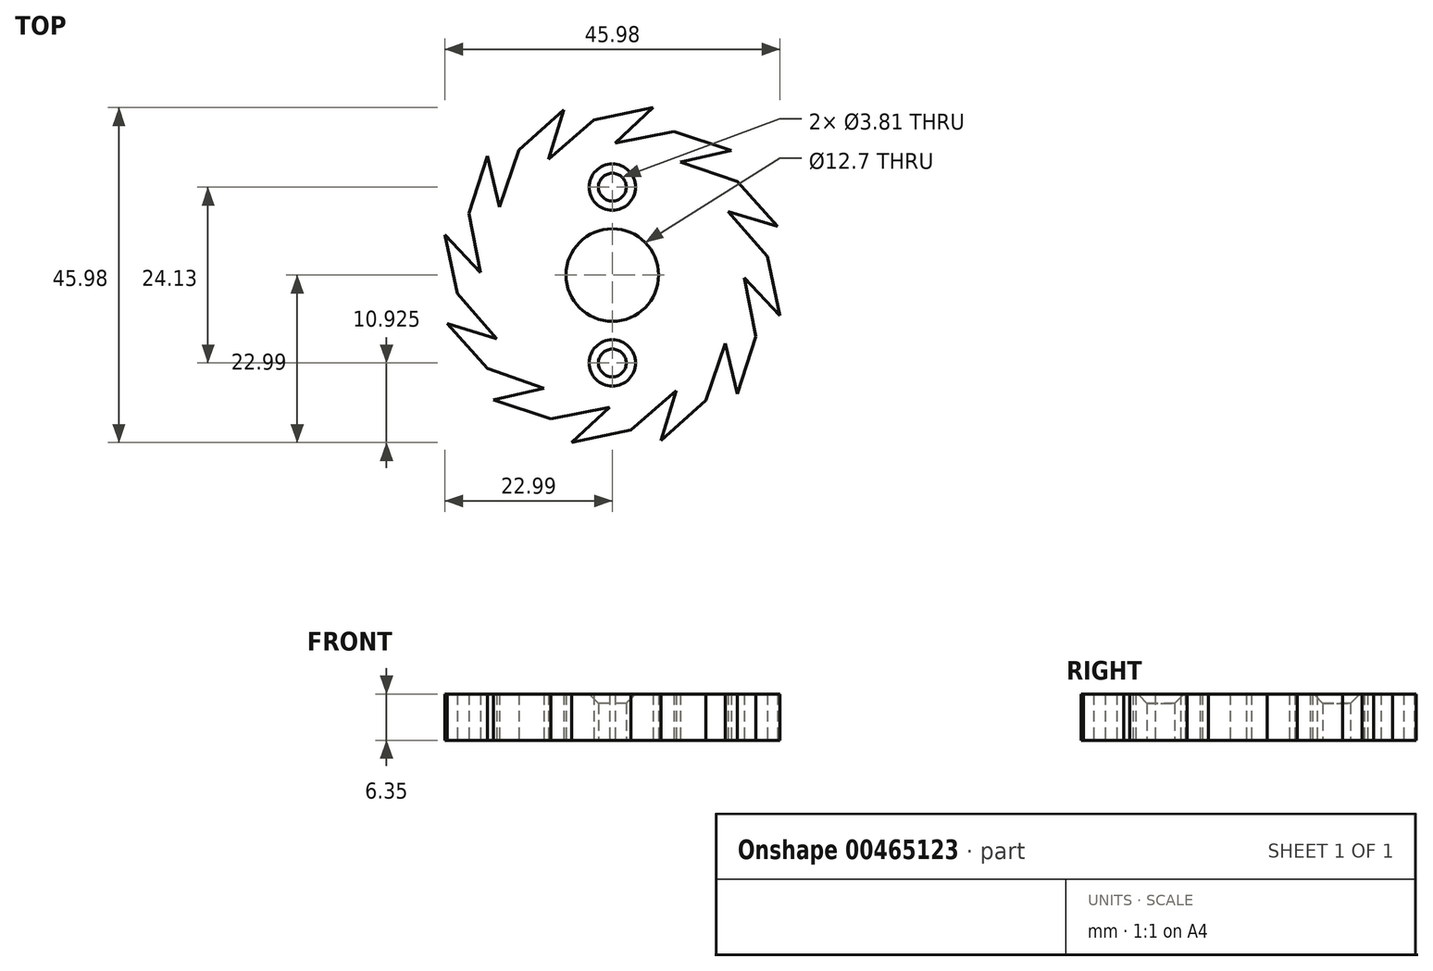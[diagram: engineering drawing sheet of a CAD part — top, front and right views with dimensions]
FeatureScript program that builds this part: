
annotation { "Feature Type Name" : "Feature", "Feature Type Description" : "" }
export const myFeature = defineFeature(function(context is Context, id is Id, definition is map)
    precondition{}
    {
        {
            var Q0;
            Q0=qCreatedBy(makeId("Top.planeOp"),FACE);
            var sketch = newSketch(context, id + "F0", { "sketchPlane" : qUnion([Q0])});
            skCircle(sketch, "E0", {"center": v(0, 0) * mm, "radius": 17.78 * mm});
            skPoint(sketch, "E1.center", {"position": v(2.36, 2.72) * mm});
            skCircle(sketch, "E2", {"center": v(0, 0) * mm, "radius": 6.35 * mm});
            skLineSegment(sketch, "E3", {"start": v(0, 6.35) * mm, "end": v(0, 17.78) * mm});
            skLineSegment(sketch, "E4", {"start": v(0, -6.35) * mm, "end": v(0, -17.78) * mm});
            skCircle(sketch, "E5", {"center": v(0, 12.06) * mm, "radius": 1.9 * mm});
            skCircle(sketch, "E6", {"center": v(0, -12.07) * mm, "radius": 1.9 * mm});
            skLineSegment(sketch, "E7", {"start": v(0, 17.78) * mm, "end": v(5.56, 22.99) * mm});
            skLineSegment(sketch, "E8", {"start": v(5.56, 22.99) * mm, "end": v(-2.54, 21.28) * mm});
            skLineSegment(sketch, "E9", {"start": v(-2.54, 21.28) * mm, "end": v(-10.44, 14.4) * mm});
            skLineSegment(sketch, "E10.1.0", {"start": v(-8.89, 15.4) * mm, "end": v(-6.67, 22.69) * mm});
            skLineSegment(sketch, "E10.1.1", {"start": v(-6.67, 22.69) * mm, "end": v(-12.84, 17.16) * mm});
            skLineSegment(sketch, "E10.1.2", {"start": v(-12.84, 17.16) * mm, "end": v(-16.24, 7.25) * mm});
            skLineSegment(sketch, "E10.2.0", {"start": v(-15.4, 8.89) * mm, "end": v(-17.12, 16.31) * mm});
            skLineSegment(sketch, "E10.2.1", {"start": v(-17.12, 16.31) * mm, "end": v(-19.7, 8.44) * mm});
            skLineSegment(sketch, "E10.2.2", {"start": v(-19.7, 8.44) * mm, "end": v(-17.68, -1.84) * mm});
            skLineSegment(sketch, "E10.3.0", {"start": v(-17.78, 0) * mm, "end": v(-22.99, 5.56) * mm});
            skLineSegment(sketch, "E10.3.1", {"start": v(-22.99, 5.56) * mm, "end": v(-21.28, -2.54) * mm});
            skLineSegment(sketch, "E10.3.2", {"start": v(-21.28, -2.54) * mm, "end": v(-14.4, -10.44) * mm});
            skLineSegment(sketch, "E10.4.0", {"start": v(-15.4, -8.89) * mm, "end": v(-22.69, -6.67) * mm});
            skLineSegment(sketch, "E10.4.1", {"start": v(-22.69, -6.67) * mm, "end": v(-17.16, -12.84) * mm});
            skLineSegment(sketch, "E10.4.2", {"start": v(-17.16, -12.84) * mm, "end": v(-7.25, -16.24) * mm});
            skLineSegment(sketch, "E10.5.0", {"start": v(-8.89, -15.4) * mm, "end": v(-16.31, -17.12) * mm});
            skLineSegment(sketch, "E10.5.1", {"start": v(-16.31, -17.12) * mm, "end": v(-8.44, -19.7) * mm});
            skLineSegment(sketch, "E10.5.2", {"start": v(-8.44, -19.7) * mm, "end": v(1.84, -17.68) * mm});
            skLineSegment(sketch, "E10.6.0", {"start": v(0, -17.78) * mm, "end": v(-5.56, -22.99) * mm});
            skLineSegment(sketch, "E10.6.1", {"start": v(-5.56, -22.99) * mm, "end": v(2.54, -21.28) * mm});
            skLineSegment(sketch, "E10.6.2", {"start": v(2.54, -21.28) * mm, "end": v(10.44, -14.4) * mm});
            skLineSegment(sketch, "E10.7.0", {"start": v(8.89, -15.4) * mm, "end": v(6.67, -22.69) * mm});
            skLineSegment(sketch, "E10.7.1", {"start": v(6.67, -22.69) * mm, "end": v(12.84, -17.16) * mm});
            skLineSegment(sketch, "E10.7.2", {"start": v(12.84, -17.16) * mm, "end": v(16.24, -7.25) * mm});
            skLineSegment(sketch, "E10.8.0", {"start": v(15.4, -8.9) * mm, "end": v(17.12, -16.31) * mm});
            skLineSegment(sketch, "E10.8.1", {"start": v(17.12, -16.31) * mm, "end": v(19.7, -8.44) * mm});
            skLineSegment(sketch, "E10.8.2", {"start": v(19.7, -8.44) * mm, "end": v(17.68, 1.84) * mm});
            skLineSegment(sketch, "E10.9.0", {"start": v(17.78, 0) * mm, "end": v(22.99, -5.56) * mm});
            skLineSegment(sketch, "E10.9.1", {"start": v(22.99, -5.56) * mm, "end": v(21.28, 2.54) * mm});
            skLineSegment(sketch, "E10.9.2", {"start": v(21.28, 2.54) * mm, "end": v(14.4, 10.44) * mm});
            skLineSegment(sketch, "E10.10.0", {"start": v(15.4, 8.89) * mm, "end": v(22.69, 6.67) * mm});
            skLineSegment(sketch, "E10.10.1", {"start": v(22.69, 6.67) * mm, "end": v(17.16, 12.84) * mm});
            skLineSegment(sketch, "E10.10.2", {"start": v(17.16, 12.84) * mm, "end": v(7.25, 16.24) * mm});
            skLineSegment(sketch, "E10.11.0", {"start": v(8.9, 15.4) * mm, "end": v(16.31, 17.12) * mm});
            skLineSegment(sketch, "E10.11.1", {"start": v(16.31, 17.12) * mm, "end": v(8.44, 19.7) * mm});
            skLineSegment(sketch, "E10.11.2", {"start": v(8.44, 19.7) * mm, "end": v(-1.84, 17.68) * mm});
            skSolve(sketch);
        }
        {
            var Q0;
            {var subQ3=sQuery(id+"F0.wireOp",EDGE,"E1.5.0");var subQ7=sQuery(id+"F0.wireOp",EDGE,"E0");var subQ8=makeQuery(id+"F0.imprint","INTERSECT",VERTEX,{"derivedFrom":[subQ7,subQ3]});Q0=makeQuery(id+"F0.imprint","IMPRINT",FACE,{"disambiguationData":[TD([[makeQuery(id+"F0.imprint","IMPRINT",EDGE,{"disambiguationData":[TD([[subQ8,-1.0]])],"derivedFrom":subQ7}),-1.0]])]});}
            var Q1;
            {var subQ3=sQuery(id+"F0.wireOp",EDGE,"E1.1.0");var subQ7=sQuery(id+"F0.wireOp",EDGE,"E0");var subQ8=makeQuery(id+"F0.imprint","INTERSECT",VERTEX,{"derivedFrom":[subQ7,subQ3]});Q1=makeQuery(id+"F0.imprint","IMPRINT",FACE,{"disambiguationData":[TD([[makeQuery(id+"F0.imprint","IMPRINT",EDGE,{"disambiguationData":[TD([[subQ8,-1.0]])],"derivedFrom":subQ7}),-1.0]])]});}
            var Q2;
            {var subQ3=sQuery(id+"F0.wireOp",EDGE,"XDNQqefp-l6QH-Php1-q7ec-htYRLLk1gTAw");var subQ5=sQuery(id+"F0.wireOp",EDGE,"E0");var subQ6=makeQuery(id+"F0.imprint","INTERSECT",VERTEX,{"derivedFrom":[subQ5,subQ3]});Q2=makeQuery(id+"F0.imprint","IMPRINT",FACE,{"disambiguationData":[TD([[makeQuery(id+"F0.imprint","IMPRINT",EDGE,{"disambiguationData":[TD([[subQ6,-1.0]])],"derivedFrom":subQ5}),-1.0]])]});}
            var Q3;
            {var subQ3=sQuery(id+"F0.wireOp",EDGE,"E1.7.0");var subQ5=sQuery(id+"F0.wireOp",EDGE,"E0");var subQ6=makeQuery(id+"F0.imprint","INTERSECT",VERTEX,{"derivedFrom":[subQ5,subQ3]});Q3=makeQuery(id+"F0.imprint","IMPRINT",FACE,{"disambiguationData":[TD([[makeQuery(id+"F0.imprint","IMPRINT",EDGE,{"disambiguationData":[TD([[subQ6,-1.0]])],"derivedFrom":subQ5}),-1.0]])]});}
            var Q4;
            {var subQ5=sQuery(id+"F0.wireOp",EDGE,"E1.8.0");var subQ6=sQuery(id+"F0.wireOp",EDGE,"E0");var subQ7=makeQuery(id+"F0.imprint","INTERSECT",VERTEX,{"derivedFrom":[subQ6,subQ5]});Q4=makeQuery(id+"F0.imprint","IMPRINT",FACE,{"disambiguationData":[TD([[makeQuery(id+"F0.imprint","IMPRINT",EDGE,{"disambiguationData":[TD([[subQ7,-1.0]])],"derivedFrom":subQ6}),-1.0]])]});}
            var Q5;
            {var subQ0=sQuery(id+"F0.wireOp",EDGE,"E1.9.0");var subQ1=sQuery(id+"F0.wireOp",EDGE,"E0");var subQ2=makeQuery(id+"F0.imprint","INTERSECT",VERTEX,{"derivedFrom":[subQ1,subQ0]});Q5=makeQuery(id+"F0.imprint","IMPRINT",FACE,{"disambiguationData":[TD([[makeQuery(id+"F0.imprint","IMPRINT",EDGE,{"disambiguationData":[TD([[subQ2,1.0]])],"derivedFrom":subQ0}),-1.0]])]});}
            var Q6;
            {var subQ3=sQuery(id+"F0.wireOp",EDGE,"E1.1.1");var subQ5=sQuery(id+"F0.wireOp",EDGE,"E0");var subQ6=makeQuery(id+"F0.imprint","INTERSECT",VERTEX,{"derivedFrom":[subQ5,subQ3]});Q6=makeQuery(id+"F0.imprint","IMPRINT",FACE,{"disambiguationData":[TD([[makeQuery(id+"F0.imprint","IMPRINT",EDGE,{"disambiguationData":[TD([[subQ6,1.0]])],"derivedFrom":subQ5}),-1.0]])]});}
            var Q7;
            {var subQ0=sQuery(id+"F0.wireOp",EDGE,"E0");var subQ11=makeQuery(id+"F0.imprint","INTERSECT",VERTEX,{"derivedFrom":[subQ0,sQuery(id+"F0.wireOp",EDGE,"E1.7.0")]});Q7=makeQuery(id+"F0.imprint","IMPRINT",FACE,{"disambiguationData":[TD([[makeQuery(id+"F0.imprint","IMPRINT",EDGE,{"disambiguationData":[TD([[subQ11,-1.0]])],"derivedFrom":subQ0}),1.0]])]});}
            var Q8;
            {var subQ3=sQuery(id+"F0.wireOp",EDGE,"E1.2.0");var subQ7=sQuery(id+"F0.wireOp",EDGE,"E0");var subQ8=makeQuery(id+"F0.imprint","INTERSECT",VERTEX,{"derivedFrom":[subQ7,subQ3]});Q8=makeQuery(id+"F0.imprint","IMPRINT",FACE,{"disambiguationData":[TD([[makeQuery(id+"F0.imprint","IMPRINT",EDGE,{"disambiguationData":[TD([[subQ8,-1.0]])],"derivedFrom":subQ7}),-1.0]])]});}
            var Q9;
            {var subQ0=sQuery(id+"F0.wireOp",EDGE,"E0");var subQ15=makeQuery(id+"F0.imprint","INTERSECT",VERTEX,{"derivedFrom":[subQ0,sQuery(id+"F0.wireOp",EDGE,"E1.1.1")]});Q9=makeQuery(id+"F0.imprint","IMPRINT",FACE,{"disambiguationData":[TD([[makeQuery(id+"F0.imprint","IMPRINT",EDGE,{"disambiguationData":[TD([[subQ15,1.0]])],"derivedFrom":subQ0}),1.0]])]});}
            var Q10;
            {var subQ3=sQuery(id+"F0.wireOp",EDGE,"E1.6.0");var subQ5=sQuery(id+"F0.wireOp",EDGE,"E0");var subQ6=makeQuery(id+"F0.imprint","INTERSECT",VERTEX,{"derivedFrom":[subQ5,subQ3]});Q10=makeQuery(id+"F0.imprint","IMPRINT",FACE,{"disambiguationData":[TD([[makeQuery(id+"F0.imprint","IMPRINT",EDGE,{"disambiguationData":[TD([[subQ6,-1.0]])],"derivedFrom":subQ5}),-1.0]])]});}
            var Q11;
            {var subQ5=sQuery(id+"F0.wireOp",EDGE,"E1.4.0");var subQ6=sQuery(id+"F0.wireOp",EDGE,"E0");var subQ7=makeQuery(id+"F0.imprint","INTERSECT",VERTEX,{"derivedFrom":[subQ6,subQ5]});Q11=makeQuery(id+"F0.imprint","IMPRINT",FACE,{"disambiguationData":[TD([[makeQuery(id+"F0.imprint","IMPRINT",EDGE,{"disambiguationData":[TD([[subQ7,-1.0]])],"derivedFrom":subQ6}),-1.0]])]});}
            var Q12;
            {var subQ3=sQuery(id+"F0.wireOp",EDGE,"E1.3.0");var subQ5=sQuery(id+"F0.wireOp",EDGE,"E0");var subQ6=makeQuery(id+"F0.imprint","INTERSECT",VERTEX,{"derivedFrom":[subQ5,subQ3]});Q12=makeQuery(id+"F0.imprint","IMPRINT",FACE,{"disambiguationData":[TD([[makeQuery(id+"F0.imprint","IMPRINT",EDGE,{"disambiguationData":[TD([[subQ6,-1.0]])],"derivedFrom":subQ5}),-1.0]])]});}
            var Q13;
            {var subQ0=sQuery(id+"F0.wireOp",EDGE,"E1.4.0");var subQ1=sQuery(id+"F0.wireOp",EDGE,"E0");var subQ2=makeQuery(id+"F0.imprint","INTERSECT",VERTEX,{"derivedFrom":[subQ1,subQ0]});Q13=makeQuery(id+"F0.imprint","IMPRINT",FACE,{"disambiguationData":[TD([[makeQuery(id+"F0.imprint","IMPRINT",EDGE,{"disambiguationData":[TD([[subQ2,1.0]])],"derivedFrom":subQ1}),-1.0]])]});}
            var Q14;
            {var subQ0=sQuery(id+"F0.wireOp",EDGE,"E1.1.0");var subQ1=sQuery(id+"F0.wireOp",EDGE,"E0");var subQ2=makeQuery(id+"F0.imprint","INTERSECT",VERTEX,{"derivedFrom":[subQ1,subQ0]});Q14=makeQuery(id+"F0.imprint","IMPRINT",FACE,{"disambiguationData":[TD([[makeQuery(id+"F0.imprint","IMPRINT",EDGE,{"disambiguationData":[TD([[subQ2,1.0]])],"derivedFrom":subQ1}),-1.0]])]});}
            var Q15;
            {var subQ0=sQuery(id+"F0.wireOp",EDGE,"E1.2.0");var subQ1=sQuery(id+"F0.wireOp",EDGE,"E0");var subQ2=makeQuery(id+"F0.imprint","INTERSECT",VERTEX,{"derivedFrom":[subQ1,subQ0]});Q15=makeQuery(id+"F0.imprint","IMPRINT",FACE,{"disambiguationData":[TD([[makeQuery(id+"F0.imprint","IMPRINT",EDGE,{"disambiguationData":[TD([[subQ2,1.0]])],"derivedFrom":subQ1}),-1.0]])]});}
            var Q16;
            {var subQ0=sQuery(id+"F0.wireOp",EDGE,"E1.8.0");var subQ1=sQuery(id+"F0.wireOp",EDGE,"E0");var subQ2=makeQuery(id+"F0.imprint","INTERSECT",VERTEX,{"derivedFrom":[subQ1,subQ0]});Q16=makeQuery(id+"F0.imprint","IMPRINT",FACE,{"disambiguationData":[TD([[makeQuery(id+"F0.imprint","IMPRINT",EDGE,{"disambiguationData":[TD([[subQ2,1.0]])],"derivedFrom":subQ1}),-1.0]])]});}
            var Q17;
            {var subQ0=sQuery(id+"F0.wireOp",EDGE,"E1.9.0");var subQ1=sQuery(id+"F0.wireOp",EDGE,"E0");var subQ2=makeQuery(id+"F0.imprint","INTERSECT",VERTEX,{"derivedFrom":[subQ1,subQ0]});Q17=makeQuery(id+"F0.imprint","IMPRINT",FACE,{"disambiguationData":[TD([[makeQuery(id+"F0.imprint","IMPRINT",EDGE,{"disambiguationData":[TD([[subQ2,1.0]])],"derivedFrom":subQ1}),-1.0]])]});}
            var Q18;
            {var subQ1=sQuery(id+"F0.wireOp",EDGE,"E0");var subQ3=sQuery(id+"F0.wireOp",EDGE,"E1.10.0");var subQ4=makeQuery(id+"F0.imprint","INTERSECT",VERTEX,{"derivedFrom":[subQ1,subQ3]});Q18=makeQuery(id+"F0.imprint","IMPRINT",FACE,{"disambiguationData":[TD([[makeQuery(id+"F0.imprint","IMPRINT",EDGE,{"disambiguationData":[TD([[subQ4,1.0]])],"derivedFrom":subQ3}),1.0]])]});}
            var Q19;
            {var subQ0=sQuery(id+"F0.wireOp",EDGE,"XDNQqefp-l6QH-Php1-q7ec-htYRLLk1gTAw");var subQ1=sQuery(id+"F0.wireOp",EDGE,"E0");var subQ2=makeQuery(id+"F0.imprint","INTERSECT",VERTEX,{"derivedFrom":[subQ1,subQ0]});Q19=makeQuery(id+"F0.imprint","IMPRINT",FACE,{"disambiguationData":[TD([[makeQuery(id+"F0.imprint","IMPRINT",EDGE,{"disambiguationData":[TD([[subQ2,1.0]])],"derivedFrom":subQ1}),-1.0]])]});}
            var Q20;
            {var subQ0=sQuery(id+"F0.wireOp",EDGE,"E1.6.0");var subQ1=sQuery(id+"F0.wireOp",EDGE,"E0");var subQ2=makeQuery(id+"F0.imprint","INTERSECT",VERTEX,{"derivedFrom":[subQ1,subQ0]});Q20=makeQuery(id+"F0.imprint","IMPRINT",FACE,{"disambiguationData":[TD([[makeQuery(id+"F0.imprint","IMPRINT",EDGE,{"disambiguationData":[TD([[subQ2,1.0]])],"derivedFrom":subQ1}),-1.0]])]});}
            var Q21;
            {var subQ0=sQuery(id+"F0.wireOp",EDGE,"E1.5.0");var subQ1=sQuery(id+"F0.wireOp",EDGE,"E0");var subQ2=makeQuery(id+"F0.imprint","INTERSECT",VERTEX,{"derivedFrom":[subQ1,subQ0]});Q21=makeQuery(id+"F0.imprint","IMPRINT",FACE,{"disambiguationData":[TD([[makeQuery(id+"F0.imprint","IMPRINT",EDGE,{"disambiguationData":[TD([[subQ2,1.0]])],"derivedFrom":subQ1}),-1.0]])]});}
            var Q22;
            {var subQ0=sQuery(id+"F0.wireOp",EDGE,"E1.3.0");var subQ1=sQuery(id+"F0.wireOp",EDGE,"E0");var subQ2=makeQuery(id+"F0.imprint","INTERSECT",VERTEX,{"derivedFrom":[subQ1,subQ0]});Q22=makeQuery(id+"F0.imprint","IMPRINT",FACE,{"disambiguationData":[TD([[makeQuery(id+"F0.imprint","IMPRINT",EDGE,{"disambiguationData":[TD([[subQ2,1.0]])],"derivedFrom":subQ1}),-1.0]])]});}
            var Q23;
            {var subQ0=sQuery(id+"F0.wireOp",EDGE,"E1.7.0");var subQ1=sQuery(id+"F0.wireOp",EDGE,"E0");var subQ2=makeQuery(id+"F0.imprint","INTERSECT",VERTEX,{"derivedFrom":[subQ1,subQ0]});Q23=makeQuery(id+"F0.imprint","IMPRINT",FACE,{"disambiguationData":[TD([[makeQuery(id+"F0.imprint","IMPRINT",EDGE,{"disambiguationData":[TD([[subQ2,1.0]])],"derivedFrom":subQ1}),-1.0]])]});}
            var Q24;
            {var subQ3=sQuery(id+"F0.wireOp",EDGE,"8bfdb414-f59d-4248-bad3-29c6685c9aad.1.0");var subQ5=sQuery(id+"F0.wireOp",EDGE,"E0");var subQ6=makeQuery(id+"F0.imprint","INTERSECT",VERTEX,{"derivedFrom":[subQ5,subQ3]});Q24=makeQuery(id+"F0.imprint","IMPRINT",FACE,{"disambiguationData":[TD([[makeQuery(id+"F0.imprint","IMPRINT",EDGE,{"disambiguationData":[TD([[subQ6,1.0]])],"derivedFrom":subQ5}),-1.0]])]});}
            var Q25;
            {var subQ3=sQuery(id+"F0.wireOp",EDGE,"8bfdb414-f59d-4248-bad3-29c6685c9aad.10.1");var subQ5=sQuery(id+"F0.wireOp",EDGE,"E0");var subQ6=makeQuery(id+"F0.imprint","INTERSECT",VERTEX,{"derivedFrom":[subQ5,subQ3]});Q25=makeQuery(id+"F0.imprint","IMPRINT",FACE,{"disambiguationData":[TD([[makeQuery(id+"F0.imprint","IMPRINT",EDGE,{"disambiguationData":[TD([[subQ6,1.0]])],"derivedFrom":subQ3}),-1.0]])]});}
            var Q26;
            {var subQ3=sQuery(id+"F0.wireOp",EDGE,"8bfdb414-f59d-4248-bad3-29c6685c9aad.9.1");var subQ5=sQuery(id+"F0.wireOp",EDGE,"E0");var subQ6=makeQuery(id+"F0.imprint","INTERSECT",VERTEX,{"derivedFrom":[subQ5,subQ3]});Q26=makeQuery(id+"F0.imprint","IMPRINT",FACE,{"disambiguationData":[TD([[makeQuery(id+"F0.imprint","IMPRINT",EDGE,{"disambiguationData":[TD([[subQ6,-1.0]])],"derivedFrom":subQ5}),-1.0]])]});}
            var Q27;
            {var subQ5=sQuery(id+"F0.wireOp",EDGE,"8bfdb414-f59d-4248-bad3-29c6685c9aad.8.1");var subQ7=sQuery(id+"F0.wireOp",EDGE,"E0");var subQ8=makeQuery(id+"F0.imprint","INTERSECT",VERTEX,{"derivedFrom":[subQ7,subQ5]});Q27=makeQuery(id+"F0.imprint","IMPRINT",FACE,{"disambiguationData":[TD([[makeQuery(id+"F0.imprint","IMPRINT",EDGE,{"disambiguationData":[TD([[subQ8,-1.0]])],"derivedFrom":subQ7}),-1.0]])]});}
            var Q28;
            {var subQ5=sQuery(id+"F0.wireOp",EDGE,"8bfdb414-f59d-4248-bad3-29c6685c9aad.7.1");var subQ7=sQuery(id+"F0.wireOp",EDGE,"E0");var subQ8=makeQuery(id+"F0.imprint","INTERSECT",VERTEX,{"derivedFrom":[subQ7,subQ5]});Q28=makeQuery(id+"F0.imprint","IMPRINT",FACE,{"disambiguationData":[TD([[makeQuery(id+"F0.imprint","IMPRINT",EDGE,{"disambiguationData":[TD([[subQ8,-1.0]])],"derivedFrom":subQ7}),-1.0]])]});}
            var Q29;
            {var subQ3=sQuery(id+"F0.wireOp",EDGE,"8bfdb414-f59d-4248-bad3-29c6685c9aad.6.1");var subQ5=sQuery(id+"F0.wireOp",EDGE,"E0");var subQ6=makeQuery(id+"F0.imprint","INTERSECT",VERTEX,{"derivedFrom":[subQ5,subQ3]});Q29=makeQuery(id+"F0.imprint","IMPRINT",FACE,{"disambiguationData":[TD([[makeQuery(id+"F0.imprint","IMPRINT",EDGE,{"disambiguationData":[TD([[subQ6,-1.0]])],"derivedFrom":subQ5}),-1.0]])]});}
            var Q30;
            {var subQ5=sQuery(id+"F0.wireOp",EDGE,"8bfdb414-f59d-4248-bad3-29c6685c9aad.5.1");var subQ7=sQuery(id+"F0.wireOp",EDGE,"E0");var subQ8=makeQuery(id+"F0.imprint","INTERSECT",VERTEX,{"derivedFrom":[subQ7,subQ5]});Q30=makeQuery(id+"F0.imprint","IMPRINT",FACE,{"disambiguationData":[TD([[makeQuery(id+"F0.imprint","IMPRINT",EDGE,{"disambiguationData":[TD([[subQ8,-1.0]])],"derivedFrom":subQ7}),-1.0]])]});}
            var Q31;
            {var subQ5=sQuery(id+"F0.wireOp",EDGE,"8bfdb414-f59d-4248-bad3-29c6685c9aad.4.1");var subQ6=sQuery(id+"F0.wireOp",EDGE,"E0");var subQ7=makeQuery(id+"F0.imprint","INTERSECT",VERTEX,{"derivedFrom":[subQ6,subQ5]});Q31=makeQuery(id+"F0.imprint","IMPRINT",FACE,{"disambiguationData":[TD([[makeQuery(id+"F0.imprint","IMPRINT",EDGE,{"disambiguationData":[TD([[subQ7,1.0]])],"derivedFrom":subQ5}),-1.0]])]});}
            var Q32;
            {var subQ5=sQuery(id+"F0.wireOp",EDGE,"8bfdb414-f59d-4248-bad3-29c6685c9aad.3.1");var subQ7=sQuery(id+"F0.wireOp",EDGE,"E0");var subQ8=makeQuery(id+"F0.imprint","INTERSECT",VERTEX,{"derivedFrom":[subQ7,subQ5]});Q32=makeQuery(id+"F0.imprint","IMPRINT",FACE,{"disambiguationData":[TD([[makeQuery(id+"F0.imprint","IMPRINT",EDGE,{"disambiguationData":[TD([[subQ8,-1.0]])],"derivedFrom":subQ7}),-1.0]])]});}
            var Q33;
            {var subQ5=sQuery(id+"F0.wireOp",EDGE,"8bfdb414-f59d-4248-bad3-29c6685c9aad.2.1");var subQ7=sQuery(id+"F0.wireOp",EDGE,"E0");var subQ8=makeQuery(id+"F0.imprint","INTERSECT",VERTEX,{"derivedFrom":[subQ7,subQ5]});Q33=makeQuery(id+"F0.imprint","IMPRINT",FACE,{"disambiguationData":[TD([[makeQuery(id+"F0.imprint","IMPRINT",EDGE,{"disambiguationData":[TD([[subQ8,-1.0]])],"derivedFrom":subQ7}),-1.0]])]});}
            var Q34;
            {var subQ3=sQuery(id+"F0.wireOp",EDGE,"8bfdb414-f59d-4248-bad3-29c6685c9aad.1.1");var subQ5=sQuery(id+"F0.wireOp",EDGE,"E0");var subQ6=makeQuery(id+"F0.imprint","INTERSECT",VERTEX,{"derivedFrom":[subQ5,subQ3]});Q34=makeQuery(id+"F0.imprint","IMPRINT",FACE,{"disambiguationData":[TD([[makeQuery(id+"F0.imprint","IMPRINT",EDGE,{"disambiguationData":[TD([[subQ6,-1.0]])],"derivedFrom":subQ5}),-1.0]])]});}
            var Q35;
            {var subQ0=sQuery(id+"F0.wireOp",EDGE,"E10.1.1");Q35=makeQuery(id+"F0.imprint","IMPRINT",FACE,{"disambiguationData":[TD([[makeQuery(id+"F0.imprint","IMPRINT",EDGE,{"derivedFrom":subQ0}),1.0]])]});}
            var Q36;
            {var subQ1=sQuery(id+"F0.wireOp",EDGE,"E8");Q36=makeQuery(id+"F0.imprint","IMPRINT",FACE,{"disambiguationData":[TD([[makeQuery(id+"F0.imprint","IMPRINT",EDGE,{"derivedFrom":subQ1}),1.0]])]});}
            var Q37;
            {var subQ0=sQuery(id+"F0.wireOp",EDGE,"E10.11.1");Q37=makeQuery(id+"F0.imprint","IMPRINT",FACE,{"disambiguationData":[TD([[makeQuery(id+"F0.imprint","IMPRINT",EDGE,{"derivedFrom":subQ0}),1.0]])]});}
            var Q38;
            {var subQ0=sQuery(id+"F0.wireOp",EDGE,"E10.10.1");Q38=makeQuery(id+"F0.imprint","IMPRINT",FACE,{"disambiguationData":[TD([[makeQuery(id+"F0.imprint","IMPRINT",EDGE,{"derivedFrom":subQ0}),1.0]])]});}
            var Q39;
            {var subQ0=sQuery(id+"F0.wireOp",EDGE,"E10.9.1");Q39=makeQuery(id+"F0.imprint","IMPRINT",FACE,{"disambiguationData":[TD([[makeQuery(id+"F0.imprint","IMPRINT",EDGE,{"derivedFrom":subQ0}),1.0]])]});}
            var Q40;
            {var subQ0=sQuery(id+"F0.wireOp",EDGE,"E10.8.1");Q40=makeQuery(id+"F0.imprint","IMPRINT",FACE,{"disambiguationData":[TD([[makeQuery(id+"F0.imprint","IMPRINT",EDGE,{"derivedFrom":subQ0}),1.0]])]});}
            var Q41;
            {var subQ0=sQuery(id+"F0.wireOp",EDGE,"E10.7.1");Q41=makeQuery(id+"F0.imprint","IMPRINT",FACE,{"disambiguationData":[TD([[makeQuery(id+"F0.imprint","IMPRINT",EDGE,{"derivedFrom":subQ0}),1.0]])]});}
            var Q42;
            {var subQ0=sQuery(id+"F0.wireOp",EDGE,"E10.6.1");Q42=makeQuery(id+"F0.imprint","IMPRINT",FACE,{"disambiguationData":[TD([[makeQuery(id+"F0.imprint","IMPRINT",EDGE,{"derivedFrom":subQ0}),1.0]])]});}
            var Q43;
            {var subQ0=sQuery(id+"F0.wireOp",EDGE,"E10.5.1");Q43=makeQuery(id+"F0.imprint","IMPRINT",FACE,{"disambiguationData":[TD([[makeQuery(id+"F0.imprint","IMPRINT",EDGE,{"derivedFrom":subQ0}),1.0]])]});}
            var Q44;
            {var subQ0=sQuery(id+"F0.wireOp",EDGE,"E10.4.1");Q44=makeQuery(id+"F0.imprint","IMPRINT",FACE,{"disambiguationData":[TD([[makeQuery(id+"F0.imprint","IMPRINT",EDGE,{"derivedFrom":subQ0}),1.0]])]});}
            var Q45;
            {var subQ0=sQuery(id+"F0.wireOp",EDGE,"E10.3.1");Q45=makeQuery(id+"F0.imprint","IMPRINT",FACE,{"disambiguationData":[TD([[makeQuery(id+"F0.imprint","IMPRINT",EDGE,{"derivedFrom":subQ0}),1.0]])]});}
            var Q46;
            {var subQ0=sQuery(id+"F0.wireOp",EDGE,"E10.2.1");Q46=makeQuery(id+"F0.imprint","IMPRINT",FACE,{"disambiguationData":[TD([[makeQuery(id+"F0.imprint","IMPRINT",EDGE,{"derivedFrom":subQ0}),1.0]])]});}
            extrude(context, id + "F1", {"entities" : qUnion([Q0, Q1, Q2, Q3, Q4, Q5, Q6, Q7, Q8, Q9, Q10, Q11, Q12, Q13, Q14, Q15, Q16, Q17, Q18, Q19, Q20, Q21, Q22, Q23, Q24, Q25, Q26, Q27, Q28, Q29, Q30, Q31, Q32, Q33, Q34, Q35, Q36, Q37, Q38, Q39, Q40, Q41, Q42, Q43, Q44, Q45, Q46]), "depth" : 6.35 * mm, "offsetDistance" : 25.4 * mm});
        }
        {
            var Q0;
            Q0=makeQuery(id+"F1.opExtrude","CAP_EDGE",EDGE,{"disambiguationData":[OSD([sQuery(id+"F0.wireOp",EDGE,"E5")])],"isStart":false});
            var Q1;
            Q1=makeQuery(id+"F1.opExtrude","CAP_EDGE",EDGE,{"disambiguationData":[OSD([sQuery(id+"F0.wireOp",EDGE,"E6")])],"isStart":false});
            chamfer(context, id + "F2", {"entities" : qUnion([Q0, Q1]), "width" : 1.27 * mm, "tangentPropagation" : true});
        }
    });
